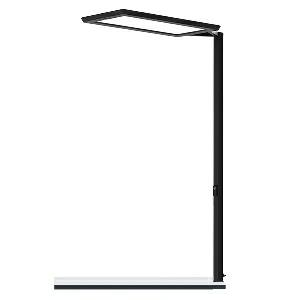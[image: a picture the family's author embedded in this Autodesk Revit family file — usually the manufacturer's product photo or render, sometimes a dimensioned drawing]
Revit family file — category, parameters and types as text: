
# Revit family: yara_single_-_yat_15000_840_r_sw_cee_00_00810173_dca8
name_source: partatom
category: Lighting Fixtures
units: mm (PartAtom-declared; Revit-internal decimal feet)

## family parameters
Cut with Voids When Loaded = No
Host = Face
Light Source = No
Part Type = Normal
Room Calculation Point = No
Round Connector Dimension = Use Diameter
Shared = No

## types (1)
- YARA.single - YAT 15000/840/R/SW/CEE/00 (1 x LED, 15000 lm, 4000K)
    Apparent Load = 107 VA
    Approval mark = CE
    CIE Flux Codes = 58 87 97 13 100
    Color Rendering = 80-89
    Color Temperature = 4000K
    Control Gear = Electronic ballast
    Default Elevation = 1800 mm
    Description = YAT 15000/840/R/SW/CEE/00/|Desk-mounted luminaire|light source: LED|work equipment: Electronic ballast DALI|connected load: 220-240 V, 50/60 Hz|Power consumption: approx. 107 W|standby: approx. 0,50|power factor: approx. 0,966|luminous flux: 15000 lm|luminous efficacy: 140 lm/W|light distribution: Direct/indirect|direct ratio: approx. 13 %|colour temperature: Cold white, ca. 4000 K|color rendering index (CRI): >= 80|chromaticity tolerance:  3 SDCM|technology: Presence and daylight sensor control (PIR)|operation: Wireless switch|luminaire body|material: Aluminium/plastic|surface: Powder coatet|colour: Black|lamp cover: Acrylic (PMMA), Satine, Structured|tubular section|material: Steel tube|surface: Powder-coated|Form: Tubular section upright|colour of tubular section: Black|weight (net): approx. 7.7 kg|mains lead: 3.00 m Mains plug CEE 7/VII|Fastening: Socket, Table adaptor|glare control: Prism aperture|luminance(L65): <= 2700 cd/m|unified glare rating(4H 8H): <=  16|special features: App control, Asymmetric radiation, Direct and indirect lighting component with edge light and light guidetechnology for a homogeneous light exit, Flicker-free, Magnetic control panel, freely positionable, PIR movement and daylight sensor|Approval mark: VDE - ENEC|
    Frequency = 50 Hz, 60 Hz
    Height = 24 mm  [stored 0.0787402 ft]
    Lamp = 1 x LED
    Lamp Light Flux = 15000 lm
    Lamp count = 1
    Length = 690 mm
    Luminous efficacy = 140 lm/W
    Manufacturer = Waldmann
    ModVariant = No
    Model = 00810173
    Mounting Place = Table
    Mounting Type = Surface mounted
    Number of Poles = 1
    OnlyDefault = Yes
    Power Factor = 1
    Product Name = YARA.single - YAT 15000/840/R/SW/CEE/00
    Product group = Desk mounted luminaire
    ProductGroupID = 22
    Protection Class = Protection class I
    Protection Degree = IP 20
    RLX_Detail_Level = 1
    RLX_Emergency_Light_Flux = 0 lm
    RLX_Emergency_Type = 0
    RLX_Emergency_Type_DB = No
    RlxData = <blob elided: 61877 chars, md5=8d08cbcd>
    Socket = socket
    Standby Power = 0 W
    System Light Flux = 15000 lm
    System Power = 107 W
    Type Comments = Product without accessories
    Type Image = yat-r-sw.jpg
    URL = http://relux.com
    VarID = ---
    Voltage = 230 V
    Voltage Range = 220-240 V
    Weight = 0.00 kg
    Width = 358 mm

note: [stored X ft] marks values corroborated as IEEE doubles in the binary element streams (Revit-internal decimal feet)

## geometry (parser evidence)
native form markers: Blend x4, Sweep x15
no freeform markers — native parametric forms only
